# Revit family: Access_Door-Insulated-Cendrex-All_Surface_Types-PFI
name_source: partatom
category: Specialty Equipment
revit_build: Autodesk Revit Architecture 2013 (Build: 20130531_2115(x64)
units: mm (PartAtom-declared; Revit-internal decimal feet)

## types (17) — shared parameters
Assembly Code = C1020700
Available Options = http://cendrex.com
Ceiling Constraint = Maximum dimensions for ceiling mounted panels are 24W x 36H.
Ceiling Mounted = No
Cendrex LEED Ready Program = http://www.cendrex.com
Construction Material = Metal - Cendrex - Aluminum
Default Elevation = 0"
Description = Fire Rated Insulated Access Door for All Surface Types
Finish = Metal - Cendrex - Powder Coated White
Manufacturer = Cendrex
Model = PFI
Product Documentation Link = http://cendrex.com
Product Page URL = http://cendrex.com
URL = http://www.cendrex.com
Wall Mounted = Yes

## per-type parameters (varying)
| type | Door Height | Door Height Calc | Door Width | Door Width Calc | Height Actual | Width Actual |
| 8 x 8 | 8" | 8" | 8" | 8" | 10" | 10" |
| 10 x 10 | 10" | 10" | 10" | 10" | 12" | 12" |
| 12 x 12 | 12" | 12" | 12" | 12" | 14" | 14" |
| 14 x 14 | 14" | 14" | 14" | 14" | 16" | 16" |
| 16 x 16 | 16" | 16" | 16" | 16" | 18" | 18" |
| 18 x 18 | 18" | 18" | 18" | 18" | 20" | 20" |
| 22 x 22 | 22" | 22" | 22" | 22" | 24" | 24" |
| 22 x 30 | 30" | 30" | 22" | 22" | 32" | 24" |
| 22 x 36 | 36" | 36" | 22" | 22" | 38" | 24" |
| 24 x 24 | 24" | 24" | 24" | 24" | 26" | 26" |
| 24 x 36 | 36" | 36" | 24" | 24" | 38" | 26" |
| 24 x 48 | 48" | 48" | 24" | 24" | 50" | 26" |
| 30 x 30 | 30" | 30" | 30" | 30" | 32" | 32" |
| 32 x 32 | 32" | 32" | 32" | 32" | 34" | 34" |
| 36 x 36 | 36" | 36" | 36" | 36" | 38" | 38" |
| 48 x 48 | 48" | 48" | 48" | 48" | 50" | 50" |
| Custom | 24" | 24" | 24" | 24" | 26" | 26" |

## geometry (parser evidence)
native form markers: Blend x18, Sweep x11
no freeform markers — native parametric forms only
